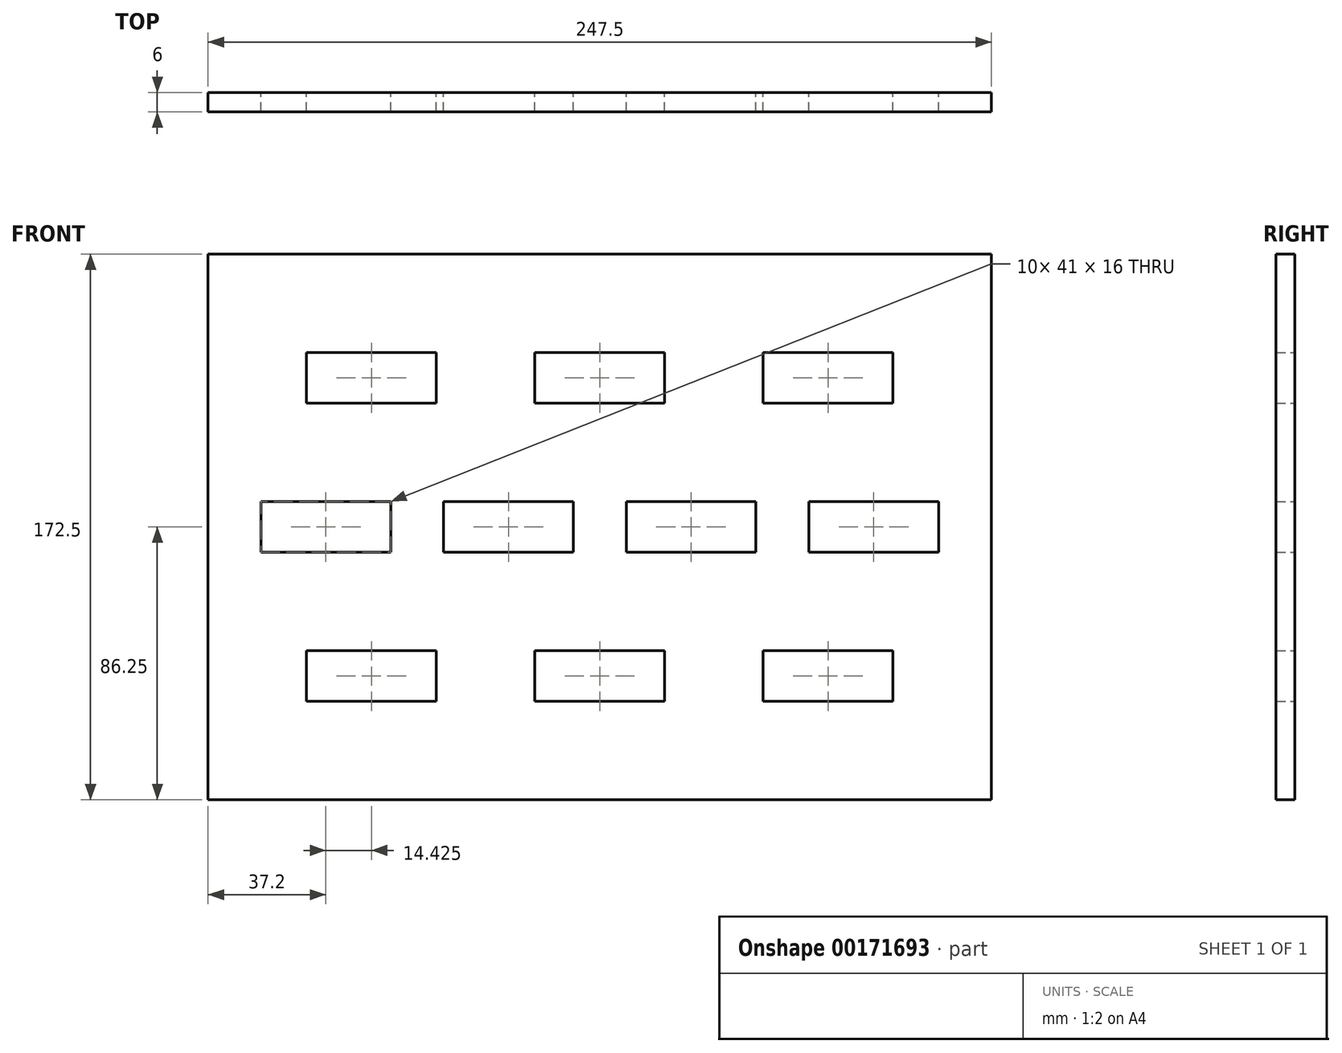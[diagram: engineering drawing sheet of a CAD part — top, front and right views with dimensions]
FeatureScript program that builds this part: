
annotation { "Feature Type Name" : "Feature", "Feature Type Description" : "" }
export const myFeature = defineFeature(function(context is Context, id is Id, definition is map)
    precondition{}
    {
        {
            var Q0;
            Q0=qCreatedBy(makeId("Front.planeOp"),FACE);
            var sketch = newSketch(context, id + "F0", { "sketchPlane" : qUnion([Q0])});
            skLineSegment(sketch, "E0.bottom", {"start": v(123.75, -86.25) * mm, "end": v(-123.75, -86.25) * mm});
            skLineSegment(sketch, "E0.top", {"start": v(123.75, 86.25) * mm, "end": v(-123.75, 86.25) * mm});
            skLineSegment(sketch, "E0.left", {"start": v(123.75, -86.25) * mm, "end": v(123.75, 86.25) * mm});
            skLineSegment(sketch, "E0.right", {"start": v(-123.75, -86.25) * mm, "end": v(-123.75, 86.25) * mm});
            skPoint(sketch, "E0.middle", {"position": v(0, 0) * mm});
            skLineSegment(sketch, "E1.bottom", {"start": v(-51.62, 39.12) * mm, "end": v(-92.62, 39.12) * mm});
            skLineSegment(sketch, "E1.top", {"start": v(-51.62, 55.12) * mm, "end": v(-92.62, 55.12) * mm});
            skLineSegment(sketch, "E1.left", {"start": v(-51.63, 39.12) * mm, "end": v(-51.63, 55.12) * mm});
            skLineSegment(sketch, "E1.right", {"start": v(-92.63, 39.12) * mm, "end": v(-92.63, 55.12) * mm});
            skPoint(sketch, "E1.middle", {"position": v(-72.12, 47.12) * mm});
            skLineSegment(sketch, "E2.bottom", {"start": v(-66.05, -8) * mm, "end": v(-107.05, -8) * mm});
            skLineSegment(sketch, "E2.top", {"start": v(-66.05, 8) * mm, "end": v(-107.05, 8) * mm});
            skLineSegment(sketch, "E2.left", {"start": v(-66.05, -8) * mm, "end": v(-66.05, 8) * mm});
            skLineSegment(sketch, "E2.right", {"start": v(-107.05, -8) * mm, "end": v(-107.05, 8) * mm});
            skPoint(sketch, "E2.middle", {"position": v(-86.55, 0) * mm});
            skLineSegment(sketch, "E3.1.0.0", {"start": v(-8.35, -8) * mm, "end": v(-49.35, -8) * mm});
            skLineSegment(sketch, "E3.1.0.1", {"start": v(-49.35, -8) * mm, "end": v(-49.35, 8) * mm});
            skLineSegment(sketch, "E3.1.0.2", {"start": v(-8.35, 8) * mm, "end": v(-49.35, 8) * mm});
            skLineSegment(sketch, "E3.1.0.3", {"start": v(-8.35, -8) * mm, "end": v(-8.35, 8) * mm});
            skLineSegment(sketch, "E3.2.0.0", {"start": v(49.35, -8) * mm, "end": v(8.35, -8) * mm});
            skLineSegment(sketch, "E3.2.0.1", {"start": v(8.35, -8) * mm, "end": v(8.35, 8) * mm});
            skLineSegment(sketch, "E3.2.0.2", {"start": v(49.35, 8) * mm, "end": v(8.35, 8) * mm});
            skLineSegment(sketch, "E3.2.0.3", {"start": v(49.35, -8) * mm, "end": v(49.35, 8) * mm});
            skLineSegment(sketch, "E3.3.0.0", {"start": v(107.05, -8) * mm, "end": v(66.05, -8) * mm});
            skLineSegment(sketch, "E3.3.0.1", {"start": v(66.05, -8) * mm, "end": v(66.05, 8) * mm});
            skLineSegment(sketch, "E3.3.0.2", {"start": v(107.05, 8) * mm, "end": v(66.05, 8) * mm});
            skLineSegment(sketch, "E3.3.0.3", {"start": v(107.05, -8) * mm, "end": v(107.05, 8) * mm});
            skLineSegment(sketch, "E3.3.0.6", {"start": v(80.48, 46.63) * mm, "end": v(152.6, 46.63) * mm, "construction": true});
            skLineSegment(sketch, "E3.direction1", {"start": v(-107.05, -8) * mm, "end": v(-49.35, -8) * mm, "construction": true});
            skLineSegment(sketch, "E4.1.0.0", {"start": v(20.5, 39.13) * mm, "end": v(-20.5, 39.12) * mm});
            skLineSegment(sketch, "E4.1.0.1", {"start": v(-20.5, 39.12) * mm, "end": v(-20.5, 55.12) * mm});
            skLineSegment(sketch, "E4.1.0.2", {"start": v(20.5, 55.12) * mm, "end": v(-20.5, 55.12) * mm});
            skLineSegment(sketch, "E4.1.0.3", {"start": v(20.5, 39.12) * mm, "end": v(20.5, 55.12) * mm});
            skLineSegment(sketch, "E4.2.0.0", {"start": v(92.63, 39.13) * mm, "end": v(51.63, 39.13) * mm});
            skLineSegment(sketch, "E4.2.0.1", {"start": v(51.62, 39.12) * mm, "end": v(51.62, 55.12) * mm});
            skLineSegment(sketch, "E4.2.0.2", {"start": v(92.63, 55.13) * mm, "end": v(51.63, 55.13) * mm});
            skLineSegment(sketch, "E4.2.0.3", {"start": v(92.62, 39.12) * mm, "end": v(92.62, 55.12) * mm});
            skLineSegment(sketch, "E4.direction1", {"start": v(-92.62, 39.12) * mm, "end": v(-20.5, 39.12) * mm, "construction": true});
            skLineSegment(sketch, "E5.MirrorCS", {"start": v(-51.62, -39.12) * mm, "end": v(-92.62, -39.12) * mm});
            skLineSegment(sketch, "E6.MirrorCS", {"start": v(92.63, -39.12) * mm, "end": v(51.63, -39.12) * mm});
            skLineSegment(sketch, "E7.MirrorCS", {"start": v(51.62, -39.12) * mm, "end": v(51.62, -55.12) * mm});
            skLineSegment(sketch, "E8.MirrorCS", {"start": v(-51.63, -39.12) * mm, "end": v(-51.63, -55.12) * mm});
            skPoint(sketch, "E9.MirrorP", {"position": v(-72.12, -47.12) * mm});
            skLineSegment(sketch, "E10.MirrorCS", {"start": v(-51.62, -55.13) * mm, "end": v(-92.62, -55.13) * mm});
            skLineSegment(sketch, "E11.MirrorCS", {"start": v(92.63, -55.12) * mm, "end": v(51.63, -55.13) * mm});
            skLineSegment(sketch, "E12.MirrorCS", {"start": v(20.5, -39.12) * mm, "end": v(-20.5, -39.12) * mm});
            skLineSegment(sketch, "E13.MirrorCS", {"start": v(-92.62, -39.12) * mm, "end": v(-20.5, -39.12) * mm, "construction": true});
            skLineSegment(sketch, "E14.MirrorCS", {"start": v(80.48, -46.63) * mm, "end": v(152.6, -46.63) * mm, "construction": true});
            skLineSegment(sketch, "E15.MirrorCS", {"start": v(92.62, -39.12) * mm, "end": v(92.62, -55.12) * mm});
            skLineSegment(sketch, "E16.MirrorCS", {"start": v(20.5, -55.13) * mm, "end": v(-20.5, -55.13) * mm});
            skLineSegment(sketch, "E17.MirrorCS", {"start": v(20.5, -39.12) * mm, "end": v(20.5, -55.12) * mm});
            skLineSegment(sketch, "E18.MirrorCS", {"start": v(-20.5, -39.12) * mm, "end": v(-20.5, -55.12) * mm});
            skLineSegment(sketch, "E19.MirrorCS", {"start": v(-92.63, -39.12) * mm, "end": v(-92.63, -55.12) * mm});
            skSolve(sketch);
        }
        {
            var Q0;
            Q0 = qSketchRegion(id + "F0", true);
            extrude(context, id + "F1", {"entities" : qUnion([Q0]), "depth" : 6 * mm, "offsetDistance" : 25 * mm});
        }
    });
